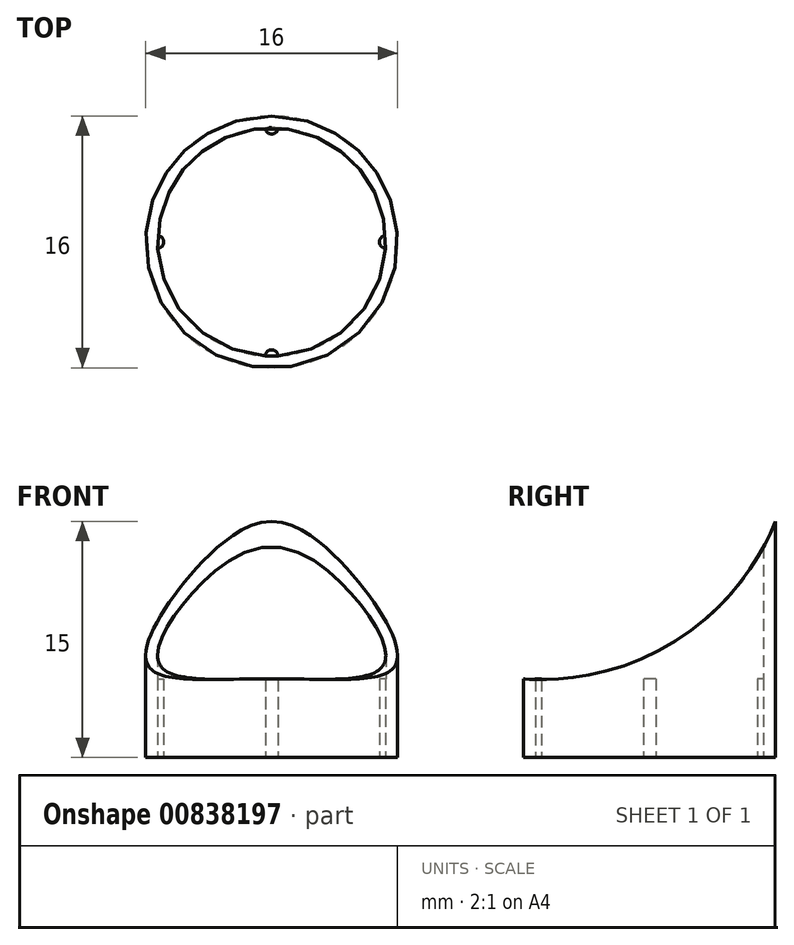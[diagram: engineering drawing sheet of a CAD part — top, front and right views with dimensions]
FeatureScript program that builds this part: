
annotation { "Feature Type Name" : "Feature", "Feature Type Description" : "" }
export const myFeature = defineFeature(function(context is Context, id is Id, definition is map)
    precondition{}
    {
        {
            var Q0;
            Q0=qCreatedBy(makeId("Top.planeOp"),FACE);
            var sketch = newSketch(context, id + "F0", { "sketchPlane" : qUnion([Q0])});
            skCircle(sketch, "E0", {"center": v(0, 0) * mm, "radius": 7.25 * mm});
            skCircle(sketch, "E1", {"center": v(0, 0) * mm, "radius": 8 * mm});
            skLineSegment(sketch, "E2", {"start": v(0, 0) * mm, "end": v(-9.33, 0) * mm, "construction": true});
            skCircle(sketch, "E3", {"center": v(-7.25, 0) * mm, "radius": 0.4 * mm});
            skCircle(sketch, "E4.1.0", {"center": v(0, -7.25) * mm, "radius": 0.4 * mm});
            skCircle(sketch, "E4.2.0", {"center": v(7.25, 0) * mm, "radius": 0.4 * mm});
            skCircle(sketch, "E5.1.3.0", {"center": v(0, 7.25) * mm, "radius": 0.4 * mm});
            skSolve(sketch);
        }
        {
            var Q0;
            Q0 = qSketchRegion(id + "F0", true);
            var Q1;
            {var subQ0=sQuery(id+"F0.wireOp",EDGE,"E3");var subQ1=sQuery(id+"F0.wireOp",EDGE,"E0");var subQ2=makeQuery(id+"F0.imprint","INTERSECT",VERTEX,{"disambiguationData":[OD(0.0)],"derivedFrom":[subQ1,subQ0]});Q1=makeQuery(id+"F0.imprint","IMPRINT",FACE,{"disambiguationData":[TD([[makeQuery(id+"F0.imprint","IMPRINT",EDGE,{"disambiguationData":[TD([[subQ2,-1.0]])],"derivedFrom":subQ1}),-1.0]])]});}
            var Q2;
            {var subQ0=sQuery(id+"F0.wireOp",EDGE,"E4.1.0");var subQ1=sQuery(id+"F0.wireOp",EDGE,"E0");var subQ2=makeQuery(id+"F0.imprint","INTERSECT",VERTEX,{"disambiguationData":[OD(0.0)],"derivedFrom":[subQ1,subQ0]});Q2=makeQuery(id+"F0.imprint","IMPRINT",FACE,{"disambiguationData":[TD([[makeQuery(id+"F0.imprint","IMPRINT",EDGE,{"disambiguationData":[TD([[subQ2,-1.0]])],"derivedFrom":subQ1}),-1.0]])]});}
            var Q3;
            {var subQ0=sQuery(id+"F0.wireOp",EDGE,"E4.2.0");var subQ1=sQuery(id+"F0.wireOp",EDGE,"E0");var subQ2=makeQuery(id+"F0.imprint","INTERSECT",VERTEX,{"disambiguationData":[OD(0.0)],"derivedFrom":[subQ1,subQ0]});Q3=makeQuery(id+"F0.imprint","IMPRINT",FACE,{"disambiguationData":[TD([[makeQuery(id+"F0.imprint","IMPRINT",EDGE,{"disambiguationData":[TD([[subQ2,1.0]])],"derivedFrom":subQ1}),-1.0]])]});}
            var Q4;
            {var subQ0=sQuery(id+"F0.wireOp",EDGE,"E5.1.3.0");var subQ1=sQuery(id+"F0.wireOp",EDGE,"E0");var subQ2=makeQuery(id+"F0.imprint","INTERSECT",VERTEX,{"disambiguationData":[OD(0.0)],"derivedFrom":[subQ1,subQ0]});Q4=makeQuery(id+"F0.imprint","IMPRINT",FACE,{"disambiguationData":[TD([[makeQuery(id+"F0.imprint","IMPRINT",EDGE,{"disambiguationData":[TD([[subQ2,-1.0]])],"derivedFrom":subQ1}),-1.0]])]});}
            extrude(context, id + "F1", {"entities" : qUnion([Q0, Q1, Q2, Q3, Q4]), "depth" : 15 * mm, "offsetDistance" : 25 * mm});
        }
        {
            var Q0;
            Q0=qCreatedBy(makeId("Right.planeOp"),FACE);
            var sketch = newSketch(context, id + "F2", { "sketchPlane" : qUnion([Q0])});
            skLineSegment(sketch, "E6", {"start": v(-8, 0) * mm, "end": v(-8, 15) * mm});
            skLineSegment(sketch, "E7.0", {"start": v(-8, 15) * mm, "end": v(8, 15) * mm});
            skLineSegment(sketch, "E8", {"start": v(-8, 5) * mm, "end": v(8, 15) * mm});
            skArc(sketch, "E9", {"start": v(-8, 5) * mm, "mid": v(1.63, 7.4) * mm, "end": v(8, 15) * mm});
            skLineSegment(sketch, "E10", {"start": v(-8, 5) * mm, "end": v(-8, 15) * mm});
            skLineSegment(sketch, "E11", {"start": v(8, 15) * mm, "end": v(-8, 15) * mm});
            skSolve(sketch);
        }
        {
            var Q0;
            {var subQ0=sQuery(id+"F2.wireOp",EDGE,"E8");var subQ1=makeQuery(id+"F2.imprint","IMPRINT",EDGE,{"derivedFrom":subQ0});var subQ4=sQuery(id+"F2.wireOp",EDGE,"E7.0");Q0=qUnion([makeQuery(id+"F2.imprint","IMPRINT",FACE,{"disambiguationData":[TD([[makeQuery(id+"F2.imprint","IMPRINT",EDGE,{"derivedFrom":subQ4}),-1.0]])]}),makeQuery(id+"F2.imprint","IMPRINT",FACE,{"disambiguationData":[TD([[subQ1,-1.0]])]})]);}
            extrude(context, id + "F3", {"entities" : qUnion([Q0]), "operationType" : NewBodyOperationType.REMOVE, "endBound" : BoundingType.SYMMETRIC, "oppositeDirection" : true, "depth" : 25 * mm, "offsetDistance" : 25 * mm});
        }
        {
            var Q0;
            {var subQ0=sQuery(id+"F0.wireOp",EDGE,"E3");var subQ1=sQuery(id+"F0.wireOp",EDGE,"E0");var subQ2=makeQuery(id+"F0.imprint","INTERSECT",VERTEX,{"disambiguationData":[OD(0.0)],"derivedFrom":[subQ1,subQ0]});Q0=makeQuery(id+"F0.imprint","IMPRINT",FACE,{"disambiguationData":[TD([[makeQuery(id+"F0.imprint","IMPRINT",EDGE,{"disambiguationData":[TD([[subQ2,-1.0]])],"derivedFrom":subQ1}),1.0]])]});}
            var Q1;
            {var subQ0=sQuery(id+"F0.wireOp",EDGE,"E4.1.0");var subQ1=sQuery(id+"F0.wireOp",EDGE,"E0");var subQ2=makeQuery(id+"F0.imprint","INTERSECT",VERTEX,{"disambiguationData":[OD(0.0)],"derivedFrom":[subQ1,subQ0]});Q1=makeQuery(id+"F0.imprint","IMPRINT",FACE,{"disambiguationData":[TD([[makeQuery(id+"F0.imprint","IMPRINT",EDGE,{"disambiguationData":[TD([[subQ2,-1.0]])],"derivedFrom":subQ1}),1.0]])]});}
            var Q2;
            {var subQ0=sQuery(id+"F0.wireOp",EDGE,"E4.2.0");var subQ1=sQuery(id+"F0.wireOp",EDGE,"E0");var subQ2=makeQuery(id+"F0.imprint","INTERSECT",VERTEX,{"disambiguationData":[OD(0.0)],"derivedFrom":[subQ1,subQ0]});Q2=makeQuery(id+"F0.imprint","IMPRINT",FACE,{"disambiguationData":[TD([[makeQuery(id+"F0.imprint","IMPRINT",EDGE,{"disambiguationData":[TD([[subQ2,1.0]])],"derivedFrom":subQ1}),1.0]])]});}
            var Q3;
            {var subQ0=sQuery(id+"F0.wireOp",EDGE,"E5.1.3.0");var subQ1=sQuery(id+"F0.wireOp",EDGE,"E0");var subQ2=makeQuery(id+"F0.imprint","INTERSECT",VERTEX,{"disambiguationData":[OD(0.0)],"derivedFrom":[subQ1,subQ0]});Q3=makeQuery(id+"F0.imprint","IMPRINT",FACE,{"disambiguationData":[TD([[makeQuery(id+"F0.imprint","IMPRINT",EDGE,{"disambiguationData":[TD([[subQ2,-1.0]])],"derivedFrom":subQ1}),1.0]])]});}
            extrude(context, id + "F4", {"entities" : qUnion([Q0, Q1, Q2, Q3]), "operationType" : NewBodyOperationType.ADD, "depth" : 5 * mm, "offsetDistance" : 25 * mm});
        }
    });
